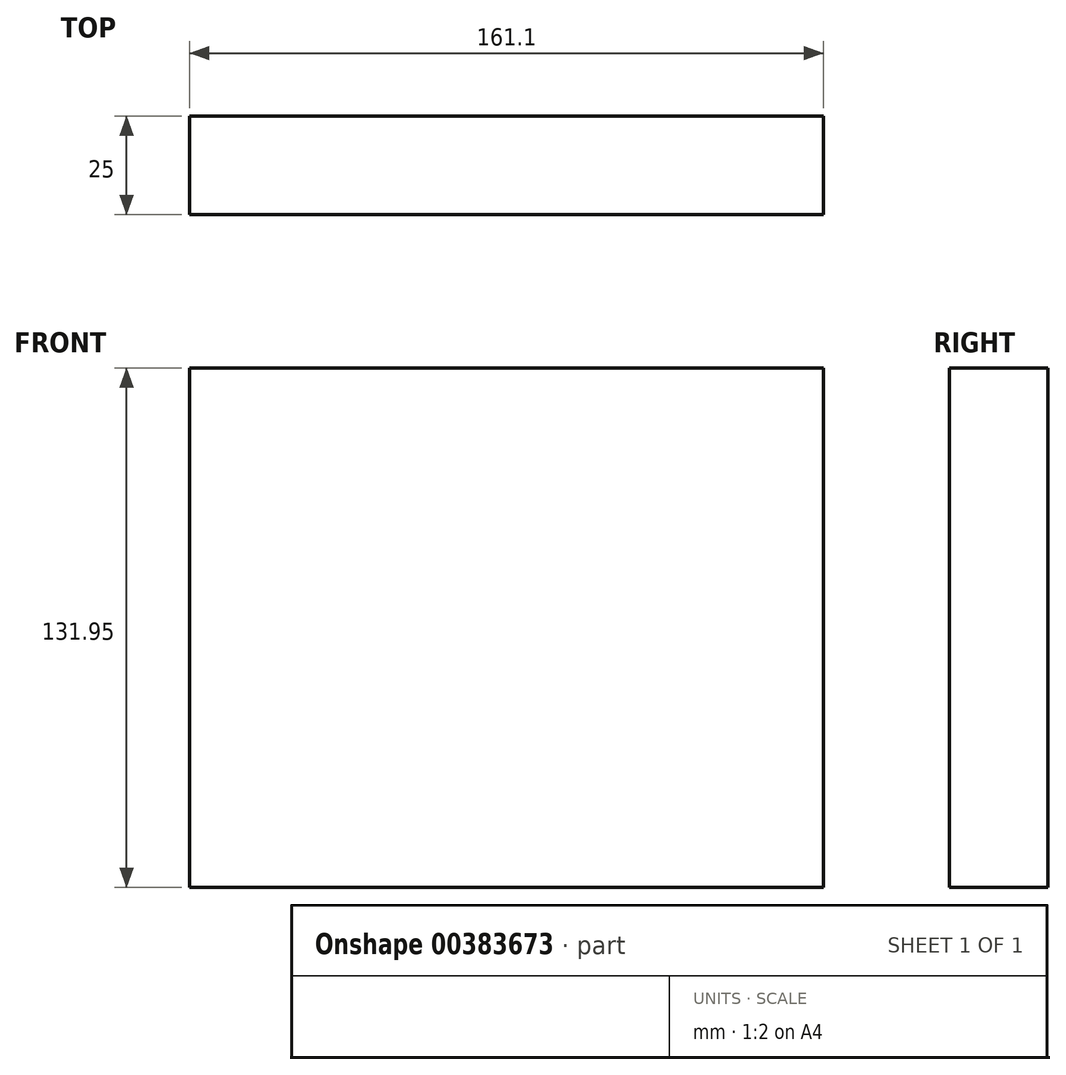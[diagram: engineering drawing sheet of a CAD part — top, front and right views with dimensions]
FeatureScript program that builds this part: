
annotation { "Feature Type Name" : "Feature", "Feature Type Description" : "" }
export const myFeature = defineFeature(function(context is Context, id is Id, definition is map)
    precondition{}
    {
        {
            var Q0;
            Q0=qCreatedBy(makeId("Front.planeOp"),FACE);
            var sketch = newSketch(context, id + "F0", { "sketchPlane" : qUnion([Q0])});
            skLineSegment(sketch, "E0.bottom", {"start": v(0, 0) * mm, "end": v(161.1, 0) * mm});
            skLineSegment(sketch, "E0.top", {"start": v(0, 131.95) * mm, "end": v(161.1, 131.95) * mm});
            skLineSegment(sketch, "E0.left", {"start": v(0, 0) * mm, "end": v(0, 131.95) * mm});
            skLineSegment(sketch, "E0.right", {"start": v(161.1, 0) * mm, "end": v(161.1, 131.95) * mm});
            skSolve(sketch);
        }
        {
            var Q0;
            Q0=makeQuery(id+"F0.imprint","IMPRINT",FACE,{"disambiguationData":[TD([[makeQuery(id+"F0.imprint","IMPRINT",EDGE,{"derivedFrom":sQuery(id+"F0.wireOp",EDGE,"E0.bottom")}),1.0]])]});
            extrude(context, id + "F1", {"entities" : qUnion([Q0]), "depth" : 25 * mm});
        }
    });
